# Revit family: BrushHolder-WCBrushHolder-WallMounted-Vitra-ArkitektaSeries-A44287+A44294
name_source: partatom
category: Plumbing Fixtures
revit_build: Autodesk Revit 2017 (Build: 20160225_1515(x64)
units: mm (PartAtom-declared; Revit-internal decimal feet)

## family parameters
Cut with Voids When Loaded = No
Host = Face
OmniClass Number = 23.45.55.17
OmniClass Title = Mixing Faucets
Part Type = Normal
Room Calculation Point = No
Round Connector Dimension = Use Diameter
Shared = Yes

## types (9) — shared parameters
BIMobject category = Accessories
CW Connection = No
Depth(mm) = 90 mm  [stored 0.295276 ft]
Design country = Turkey
HW Connection = No
Height(mm) = 366 mm
IFC Classification = Sanitary Terminal
Manufacturer = Vitra
Manufacturer name = Vitra
Masterformat 2014 Code = 10 28 13
Masterformat 2014 Description = Toilet Accessories
NBS Referans Code = 35-75-86
NBS Referans Description = Toilet Brush Holders
Nominal height = 0.000
Nominal width = 0.000
OmniClass Code = 23-31 25 00
OmniClass Description = Toilet and Bath Specialties
Product Type = Wc Brush Holder Wall
Product certification = https://vitraglobal.com
Product family = Arkitekt
Product group = Arkitekt WC Brush Holder
UNSPSC Code = 3018
UNSPSC Description = Plumbing Fixtures
URL = https://vitraglobal.com
Uniclass 1.4 Code = L7313
Uniclass 1.4 Description = Sanitary above ground pipes and fittings
Uniclass 2.0 Code = PR-35-75-86
Uniclass 2.0 Description = Toilet Brush Holders
Uniclass 2015 Code = PR_40_20_76_86
Uniclass 2015 Name = Toilet Brush Holders
Uniformat II Code = D2010
Uniformat II Description = Plumbing Fixtures
Warranty Period (Year) = 5 Years
Waste Connection = No
Weight Net (kg) = 0,650
Width(mm) = 83 mm  [stored 0.27231 ft]
Youtube = https://www.youtube.com
zero-valued in all types: Cost, Default Elevation

## per-type parameters (varying)
| type | Article No. (default) | Brand | Coating Material | Color | Description | Model | MountingType | Product SKU | Product data url | Technical description |
| BrushHolder-WCBrushHolder-WallMounted-Vitra-ArkitektaSeries-A44287 | A44287 |  | Chrome | Chrome | Arkitekt Wc Brush Holder Wall- Wall Mounted | A44287 | Wall Mounted | A44287 | https://www.vitra.com.tr | https://www.vitra.com.tr |
| BrushHolder-WCBrushHolder-FloorStanding-Vitra-ArkitektaSeries-A44294 | A44287 |  | Chrome | Chrome | Arkitekt Wc Brush Holder Wall- Floor Standing | A44287 | Floor Standing | A44287 | https://www.vitra.com.tr | https://www.vitra.com.tr |
| BrushHolder-WCBrushHolder-WallMounted-Vitra-ArkitektaSeries-A44287EXP | A44287EXP | VitrA | Chrome | Chrome | Arkitekt Wc Brush Holder Wall- Wall Mounted | A44287EXP | Wall Mounted | A44287EXP | https://www.vitraglobal.com | https://www.vitraglobal.com |
| BrushHolder-WCBrushHolder-FloorStanding-Vitra-ArkitektaSeries-A44294EXP | A44294EXP | VitrA | Chrome | Chrome | Arkitekt Wc Brush Holder Wall- Floor Standing | A44294EXP | Floor Standing | A44294EXP | https://www.vitraglobal.com | https://www.vitraglobal.com |
| BrushHolder-WCBrushHolder-WallMounted-Vitra-ArkitektaSeries-A44287TPL | A44287TPL |  | Chrome | Chrome | Arkitekt Wc Brush Holder Wall- Wall Mounted | A44287TPL | Wall Mounted | A44287TPL | https://www.vitraglobal.com | https://www.vitraglobal.com |
| BrushHolder-WCBrushHolder-WallMounted-Vitra-ArkitektaSeries-A44287TPX | A44287TPX | VitrA | Chrome | Chrome | Arkitekt Wc Brush Holder Wall- Wall Mounted | A44287TPX | Wall Mounted | A44287TPX | https://www.vitraglobal.com | https://www.vitraglobal.com |
| BrushHolder-WCBrushHolder-WallMounted-Vitra-ArkitektaSeries-A44287VUK | A44287VUK | VitrA | Chrome | Chrome | Arkitekt Wc Brush Holder Wall- Wall Mounted | A44287VUK | Wall Mounted | A44287VUK | https://www.vitraglobal.com | https://www.vitraglobal.com |
| BrushHolder-WCBrushHolder-FloorStanding-Vitra-ArkitektaSeries-A4429423 | A4429423 |  | Gold | Gold | Arkitekt Wc Brush Holder Wall- Floor Standing | A4429423 | Floor Standing | A4429423 | https://www.vitra.com.tr | https://www.vitra.com.tr |
| BrushHolder-WCBrushHolder-FloorStanding-Vitra-ArkitektaSeries-A44294IND | A44294IND | VitrA | Chrome | Chrome | Arkitekt Wc Brush Holder Wall- Floor Standing | A44294IND | Floor Standing | A44294IND | https://www.vitraglobal.com | https://www.vitraglobal.com |

note: [stored X ft] marks values corroborated as IEEE doubles in the binary element streams (Revit-internal decimal feet)

## geometry (parser evidence)
native form markers: Sweep x3
no freeform markers — native parametric forms only
